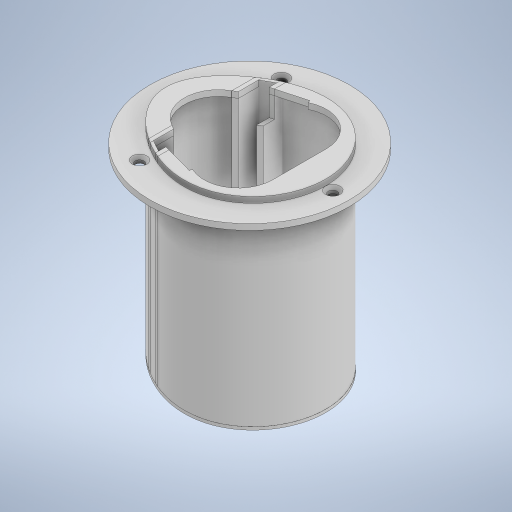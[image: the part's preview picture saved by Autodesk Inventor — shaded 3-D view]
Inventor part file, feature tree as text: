
AUTODESK INVENTOR PART (.ipt)
format: ipt  version: 2023 (Build 270158000, 158)  size: 1,648,128 bytes
history: native  units: mm
features: extrude x14, other x6, chamfer x1, sketch x1
ambient origin geometry x8: Origin, YZ Plane, XZ Plane, XY Plane, X Axis, Y Axis, Z Axis, Center Point
bodies: Volumenkörper6 (feature_tree), Volumenkörper8 (feature_tree), Volumenkörper9 (feature_tree)
feature tree (22):
  other  "Vertikale Skizze"
  extrude  "Hauptkörper oben"  Depth=2.0mm
  extrude  "Hauptkörper unten"  Depth=2.0mm
  extrude  "Hauptkörper mitte"  Depth=2.0mm
  other  "Boden"
  other  "Akkuführungslasche vertikale Skizze"
  extrude  "Akkuführungslasche"  TaperAngle=0.0deg  [1 undecoded]
  extrude  "Akkuführungslasche boolean"  Depth=66.0mm
  extrude  "Extrusion13"  TaperAngle=0.0deg  [1 undecoded]
  extrude  "Akkuführungslasche boolean außen"  Depth=2.0mm
  extrude  "Extrusion15"  TaperAngle=0.0deg  [1 undecoded]
  extrude  "Akkuführungslasche boolean hauptkörper"  TaperAngle=0.0deg  [1 undecoded]
  extrude  "Hauptkörper Außenwand oben"  TaperAngle=0.0deg  [1 undecoded]
  extrude  "Kontaktlöcher"  Depth=68.0mm
  extrude  "Akkuführungslasche boolean2"  TaperAngle=0.0deg  [1 undecoded]
  extrude  "Akkuführungslasche boolean3"  Depth=66.0mm
  extrude  "Halterungsebene"  TaperAngle=0.0deg  [1 undecoded]
  chamfer  "Schraubenlöcherabrundung"  Distance=2.0mm
  other  "Vorlage von oben"
  other  "Bild2"
  sketch  "Skizze8"  dims[d3=68.0mm d4=11.7mm d64=1.0mm d79=2.0mm d80=0.0mm d82=66.0mm d83=0.0mm d86=1.0mm d87=0.0mm d88=0.0mm d89=-66.0mm d90=0.0mm d137=68.0mm d138=0.0mm d140=66.0mm d141=0.0mm d142=2.0mm d143=0.0mm d145=66.0mm d146=0.0mm d147=2.0mm d148=0.0mm d149=2.0mm d150=0.0mm d151=2.0mm d152=0.0mm d182=10.0mm d183=0.0mm d197=7.0mm d198=0.0mm d199=2.0mm d200=0.0mm d207=3.0mm d208=3.0mm d209=3.0mm d212=2.0mm d213=0.0mm d214=1.0mm d215=2.0mm d216=45.0deg d8=0.5mm d9=0.872665mm d10=0.5mm d11=0.872665mm d99=0.5mm d100=0.872665mm d101=0.5mm d102=0.872665mm d139=0.5mm d189=0.5mm d190=0.872665mm d191=0.5mm d192=0.872665mm d193=0.5mm d194=0.872665mm d195=0.5mm d196=0.872665mm]
  other  "Bild3"
note: 7 required parameter values undecoded (feature->parameter linkage not recoverable at this tier; creation-order binding heuristic only, values carry confidence <= 0.55)
